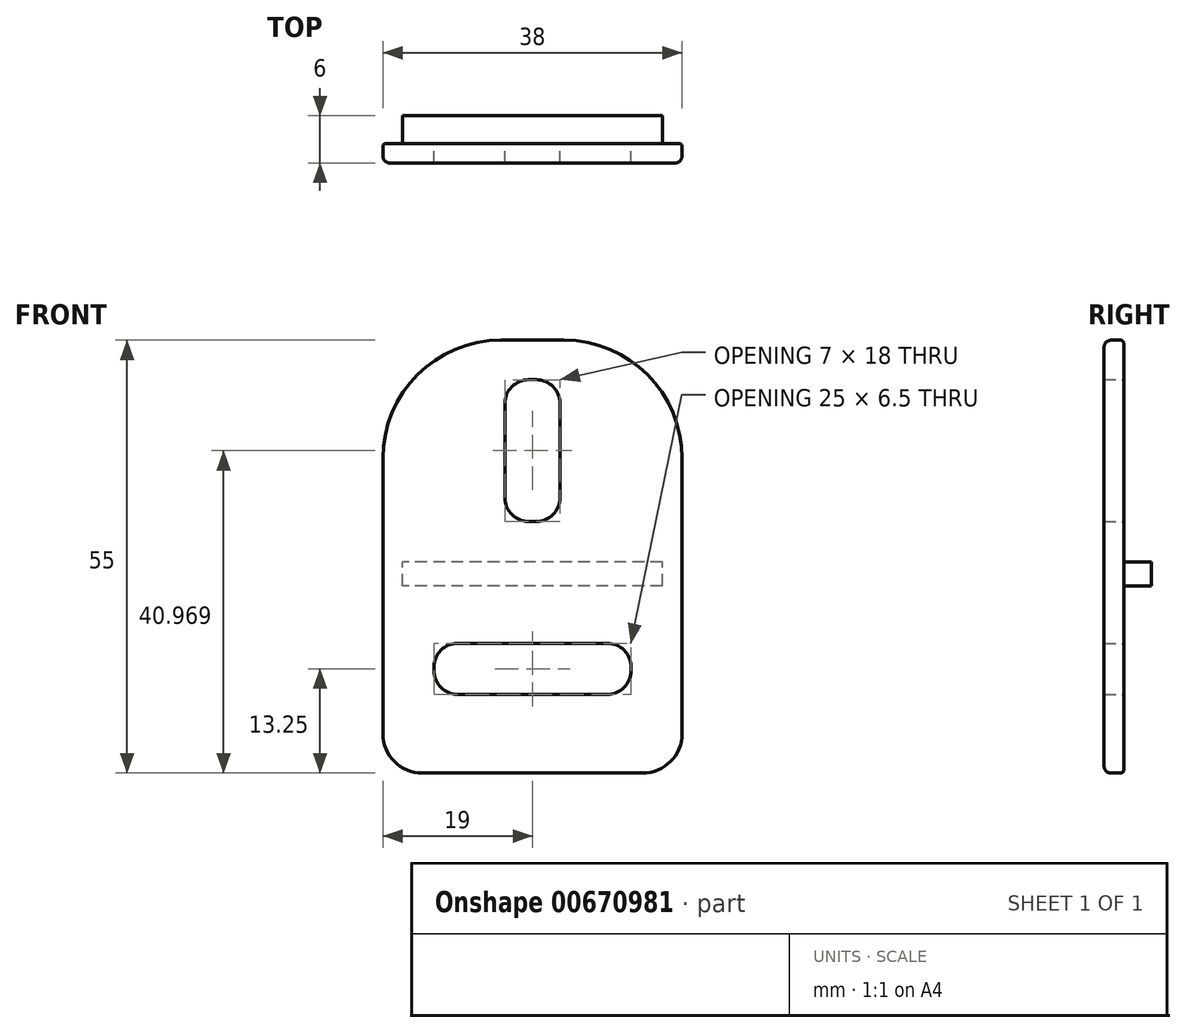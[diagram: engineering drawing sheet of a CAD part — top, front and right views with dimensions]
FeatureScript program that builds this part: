
annotation { "Feature Type Name" : "Feature", "Feature Type Description" : "" }
export const myFeature = defineFeature(function(context is Context, id is Id, definition is map)
    precondition{}
    {
        {
            var Q0;
            Q0=qCreatedBy(makeId("Front.planeOp"),FACE);
            var sketch = newSketch(context, id + "F0", { "sketchPlane" : qUnion([Q0])});
            skLineSegment(sketch, "E0.bottom", {"start": v(-19, 55) * mm, "end": v(19, 55) * mm});
            skLineSegment(sketch, "E0.top", {"start": v(-19, 0) * mm, "end": v(19, 0) * mm});
            skLineSegment(sketch, "E0.left", {"start": v(-19, 55) * mm, "end": v(-19, 0) * mm});
            skLineSegment(sketch, "E0.right", {"start": v(19, 55) * mm, "end": v(19, 0) * mm});
            skLineSegment(sketch, "E1.bottom", {"start": v(-12.5, 16.5) * mm, "end": v(12.5, 16.5) * mm});
            skLineSegment(sketch, "E1.top", {"start": v(-12.5, 10) * mm, "end": v(12.5, 10) * mm});
            skLineSegment(sketch, "E1.left", {"start": v(-12.5, 16.5) * mm, "end": v(-12.5, 10) * mm});
            skLineSegment(sketch, "E1.right", {"start": v(12.5, 16.5) * mm, "end": v(12.5, 10) * mm});
            skPoint(sketch, "E2", {"position": v(0, 10) * mm});
            skLineSegment(sketch, "E3.bottom", {"start": v(-3.5, 49.97) * mm, "end": v(3.5, 49.97) * mm});
            skLineSegment(sketch, "E3.top", {"start": v(-3.5, 31.97) * mm, "end": v(3.5, 31.97) * mm});
            skLineSegment(sketch, "E3.left", {"start": v(-3.5, 49.97) * mm, "end": v(-3.5, 31.97) * mm});
            skLineSegment(sketch, "E3.right", {"start": v(3.5, 49.97) * mm, "end": v(3.5, 31.97) * mm});
            skPoint(sketch, "E3.middle", {"position": v(0, 40.97) * mm});
            skSolve(sketch);
        }
        {
            var Q0;
            Q0 = qSketchRegion(id + "F0", true);
            extrude(context, id + "F1", {"entities" : qUnion([Q0]), "depth" : 2.5 * mm, "offsetDistance" : 25 * mm});
        }
        {
            var Q0;
            Q0=makeQuery(id+"F1.opExtrude","SWEPT_EDGE",EDGE,{"disambiguationData":[OSD([sQuery(id+"F0.wireOp",EDGE,"E0.bottom"),sQuery(id+"F0.wireOp",EDGE,"E0.left")])]});
            var Q1;
            Q1=makeQuery(id+"F1.opExtrude","SWEPT_EDGE",EDGE,{"disambiguationData":[OSD([sQuery(id+"F0.wireOp",EDGE,"E0.bottom"),sQuery(id+"F0.wireOp",EDGE,"E0.right")])]});
            fillet(context, id + "F2", {"entities" : qUnion([Q0, Q1]), "radius" : 15 * mm, "tangentPropagation" : true, "allowEdgeOverflow" : false});
        }
        {
            var Q0;
            Q0=makeQuery(id+"F1.opExtrude","SWEPT_EDGE",EDGE,{"disambiguationData":[OSD([sQuery(id+"F0.wireOp",EDGE,"E0.top"),sQuery(id+"F0.wireOp",EDGE,"E0.left")])]});
            var Q1;
            Q1=makeQuery(id+"F1.opExtrude","SWEPT_EDGE",EDGE,{"disambiguationData":[OSD([sQuery(id+"F0.wireOp",EDGE,"E0.top"),sQuery(id+"F0.wireOp",EDGE,"E0.right")])]});
            fillet(context, id + "F3", {"entities" : qUnion([Q0, Q1]), "radius" : 5 * mm, "tangentPropagation" : true, "allowEdgeOverflow" : false});
        }
        {
            var Q0;
            Q0=makeQuery(id+"F1.opExtrude","SWEPT_EDGE",EDGE,{"disambiguationData":[OSD([sQuery(id+"F0.wireOp",EDGE,"E1.top"),sQuery(id+"F0.wireOp",EDGE,"E1.left")])]});
            var Q1;
            Q1=makeQuery(id+"F1.opExtrude","SWEPT_EDGE",EDGE,{"disambiguationData":[OSD([sQuery(id+"F0.wireOp",EDGE,"E1.top"),sQuery(id+"F0.wireOp",EDGE,"E1.right")])]});
            var Q2;
            Q2=makeQuery(id+"F1.opExtrude","SWEPT_EDGE",EDGE,{"disambiguationData":[OSD([sQuery(id+"F0.wireOp",EDGE,"E1.bottom"),sQuery(id+"F0.wireOp",EDGE,"E1.right")])]});
            var Q3;
            Q3=makeQuery(id+"F1.opExtrude","SWEPT_EDGE",EDGE,{"disambiguationData":[OSD([sQuery(id+"F0.wireOp",EDGE,"E1.bottom"),sQuery(id+"F0.wireOp",EDGE,"E1.left")])]});
            var Q4;
            Q4=makeQuery(id+"F1.opExtrude","SWEPT_EDGE",EDGE,{"disambiguationData":[OSD([sQuery(id+"F0.wireOp",EDGE,"E3.bottom"),sQuery(id+"F0.wireOp",EDGE,"E3.left")])]});
            var Q5;
            Q5=makeQuery(id+"F1.opExtrude","SWEPT_EDGE",EDGE,{"disambiguationData":[OSD([sQuery(id+"F0.wireOp",EDGE,"E3.top"),sQuery(id+"F0.wireOp",EDGE,"E3.left")])]});
            var Q6;
            Q6=makeQuery(id+"F1.opExtrude","SWEPT_EDGE",EDGE,{"disambiguationData":[OSD([sQuery(id+"F0.wireOp",EDGE,"E3.top"),sQuery(id+"F0.wireOp",EDGE,"E3.right")])]});
            var Q7;
            Q7=makeQuery(id+"F1.opExtrude","SWEPT_EDGE",EDGE,{"disambiguationData":[OSD([sQuery(id+"F0.wireOp",EDGE,"E3.bottom"),sQuery(id+"F0.wireOp",EDGE,"E3.right")])]});
            fillet(context, id + "F4", {"entities" : qUnion([Q0, Q1, Q2, Q3, Q4, Q5, Q6, Q7]), "radius" : 3 * mm, "tangentPropagation" : true, "allowEdgeOverflow" : false});
        }
        {
            var Q0;
            Q0=makeQuery(id+"F1.opExtrude","CAP_FACE",FACE,{"disambiguationData":[OSD([sQuery(id+"F0.wireOp",EDGE,"E0.bottom"),sQuery(id+"F0.wireOp",EDGE,"E0.top"),sQuery(id+"F0.wireOp",EDGE,"E0.left"),sQuery(id+"F0.wireOp",EDGE,"E0.right"),sQuery(id+"F0.wireOp",EDGE,"E1.bottom"),sQuery(id+"F0.wireOp",EDGE,"E1.top"),sQuery(id+"F0.wireOp",EDGE,"E1.left"),sQuery(id+"F0.wireOp",EDGE,"E1.right"),sQuery(id+"F0.wireOp",EDGE,"E3.bottom"),sQuery(id+"F0.wireOp",EDGE,"E3.top"),sQuery(id+"F0.wireOp",EDGE,"E3.left"),sQuery(id+"F0.wireOp",EDGE,"E3.right")])],"isStart":true});
            var sketch = newSketch(context, id + "F5", { "sketchPlane" : qUnion([Q0])});
            skLineSegment(sketch, "E4.bottom", {"start": v(-16.5, 23.8) * mm, "end": v(16.5, 23.8) * mm});
            skLineSegment(sketch, "E4.top", {"start": v(-16.5, 26.8) * mm, "end": v(16.5, 26.8) * mm});
            skLineSegment(sketch, "E4.left", {"start": v(-16.5, 23.8) * mm, "end": v(-16.5, 26.8) * mm});
            skLineSegment(sketch, "E4.right", {"start": v(16.5, 23.8) * mm, "end": v(16.5, 26.8) * mm});
            skPoint(sketch, "E4.middle", {"position": v(0, 25.3) * mm});
            skSolve(sketch);
        }
        {
            var Q0;
            Q0 = qSketchRegion(id + "F5", true);
            extrude(context, id + "F6", {"entities" : qUnion([Q0]), "operationType" : NewBodyOperationType.ADD, "depth" : 3.5 * mm, "offsetDistance" : 25 * mm});
        }
        {
            var Q0;
            Q0=makeQuery(id+"F1.opExtrude","CAP_EDGE",EDGE,{"disambiguationData":[OSD([sQuery(id+"F0.wireOp",EDGE,"E0.right")])],"isStart":true});
            fillet(context, id + "F7", {"entities" : qUnion([Q0]), "radius" : .4 * mm, "tangentPropagation" : true, "allowEdgeOverflow" : false});
        }
        {
            var Q0;
            Q0=makeQuery(id+"F1.opExtrude","CAP_EDGE",EDGE,{"disambiguationData":[OSD([sQuery(id+"F0.wireOp",EDGE,"E0.right")])],"isStart":false});
            fillet(context, id + "F8", {"entities" : qUnion([Q0]), "radius" : .9 * mm, "tangentPropagation" : true, "allowEdgeOverflow" : false});
        }
    });
